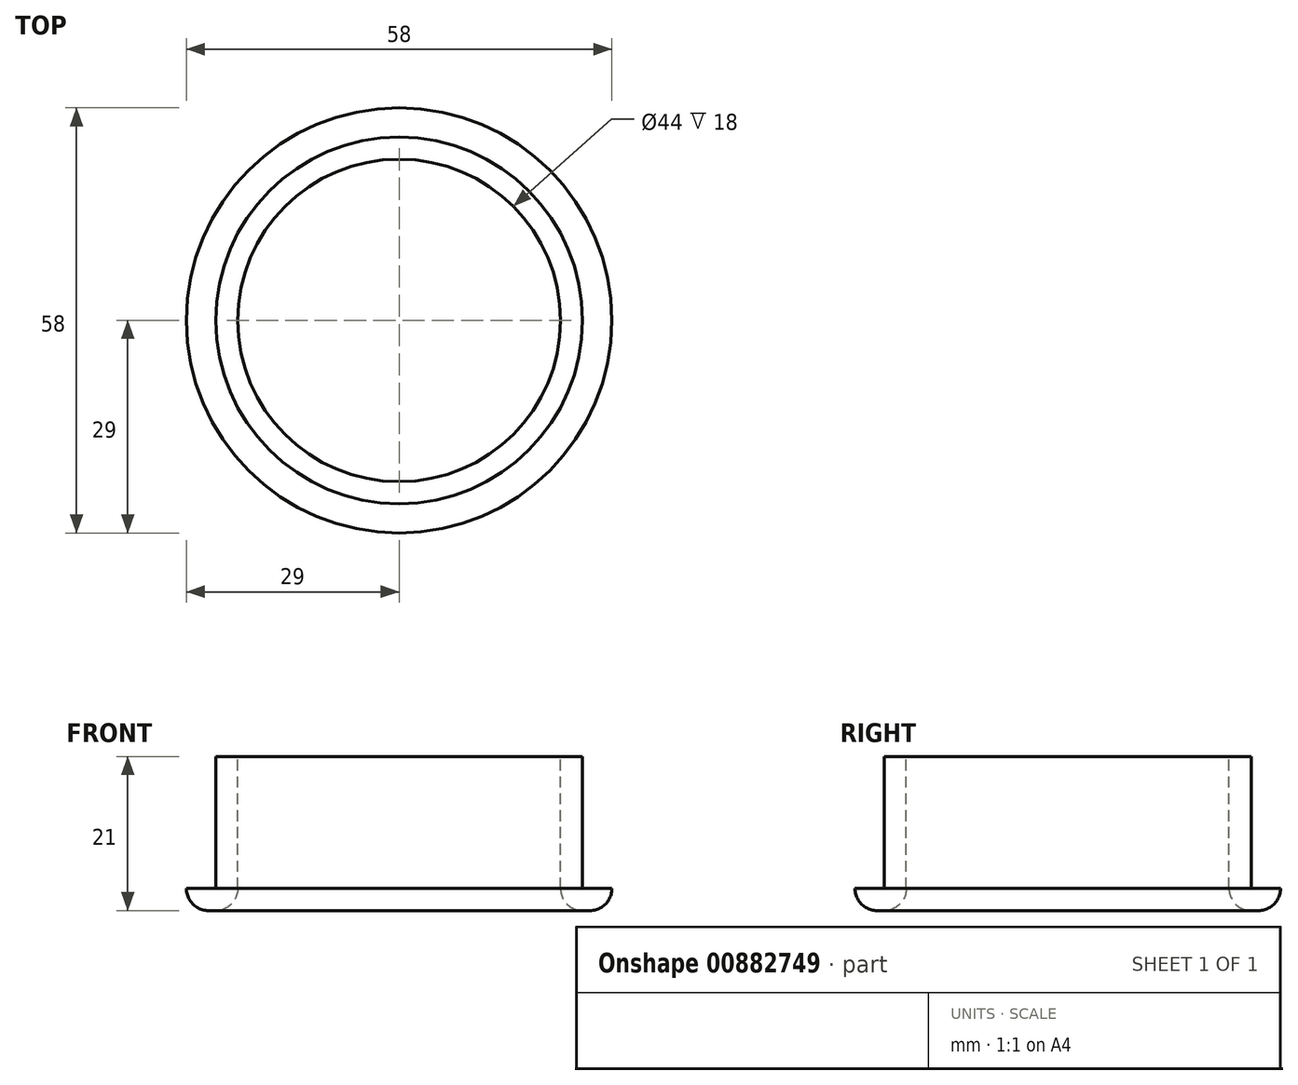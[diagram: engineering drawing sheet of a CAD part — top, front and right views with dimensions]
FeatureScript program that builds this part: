
annotation { "Feature Type Name" : "Feature", "Feature Type Description" : "" }
export const myFeature = defineFeature(function(context is Context, id is Id, definition is map)
    precondition{}
    {
        {
            var Q0;
            Q0=qCreatedBy(makeId("Top.planeOp"),FACE);
            var sketch = newSketch(context, id + "F0", { "sketchPlane" : qUnion([Q0])});
            skCircle(sketch, "E0", {"center": v(0, 0) * mm, "radius": 25 * mm});
            skSolve(sketch);
        }
        {
            var Q0;
            Q0=makeQuery(id+"F0.imprint","IMPRINT",FACE,{"disambiguationData":[TD([[makeQuery(id+"F0.imprint","IMPRINT",EDGE,{"derivedFrom":sQuery(id+"F0.wireOp",EDGE,"E0")}),1.0]])]});
            extrude(context, id + "F1", {"entities" : qUnion([Q0]), "depth" : 18 * mm, "offsetDistance" : 25 * mm});
        }
        {
            var Q0;
            Q0=qCreatedBy(makeId("Top.planeOp"),FACE);
            var sketch = newSketch(context, id + "F2", { "sketchPlane" : qUnion([Q0])});
            skCircle(sketch, "E1", {"center": v(0, 0) * mm, "radius": 29 * mm});
            skSolve(sketch);
        }
        {
            var Q0;
            Q0=makeQuery(id+"F2.imprint","IMPRINT",FACE,{"disambiguationData":[TD([[makeQuery(id+"F2.imprint","IMPRINT",EDGE,{"derivedFrom":sQuery(id+"F2.wireOp",EDGE,"E1")}),1.0]])]});
            extrude(context, id + "F3", {"entities" : qUnion([Q0]), "operationType" : NewBodyOperationType.ADD, "oppositeDirection" : true, "depth" : 3 * mm, "offsetDistance" : 25 * mm});
        }
        {
            var Q0;
            Q0=makeQuery(id+"F1.opExtrude","CAP_FACE",FACE,{"disambiguationData":[OSD([sQuery(id+"F0.wireOp",EDGE,"E0")])],"isStart":false});
            var sketch = newSketch(context, id + "F4", { "sketchPlane" : qUnion([Q0])});
            skCircle(sketch, "E2", {"center": v(0, 0) * mm, "radius": 22 * mm});
            skSolve(sketch);
        }
        {
            var Q0;
            Q0=makeQuery(id+"F4.imprint","IMPRINT",FACE,{"disambiguationData":[TD([[makeQuery(id+"F4.imprint","IMPRINT",EDGE,{"derivedFrom":sQuery(id+"F4.wireOp",EDGE,"E2")}),1.0]])]});
            extrude(context, id + "F5", {"entities" : qUnion([Q0]), "operationType" : NewBodyOperationType.REMOVE, "endBound" : BoundingType.THROUGH_ALL, "oppositeDirection" : true, "depth" : 25 * mm, "offsetDistance" : 25 * mm});
        }
        {
            var Q0;
            Q0=makeQuery(id+"F5.boolean.opBoolean","INTERSECT",EDGE,{"derivedFrom":[makeQuery(id+"F3.opExtrude","CAP_FACE",FACE,{"disambiguationData":[OSD([sQuery(id+"F2.wireOp",EDGE,"E1")])],"isStart":false}),makeQuery(id+"F5.opExtrude","SWEPT_FACE",FACE,{"disambiguationData":[OSD([sQuery(id+"F4.wireOp",EDGE,"E2")])]})]});
            var Q1;
            Q1=makeQuery(id+"F3.opExtrude","CAP_EDGE",EDGE,{"disambiguationData":[OSD([sQuery(id+"F2.wireOp",EDGE,"E1")])],"isStart":false});
            fillet(context, id + "F6", {"entities" : qUnion([Q0, Q1]), "radius" : 3 * mm, "tangentPropagation" : true, "allowEdgeOverflow" : false});
        }
    });
